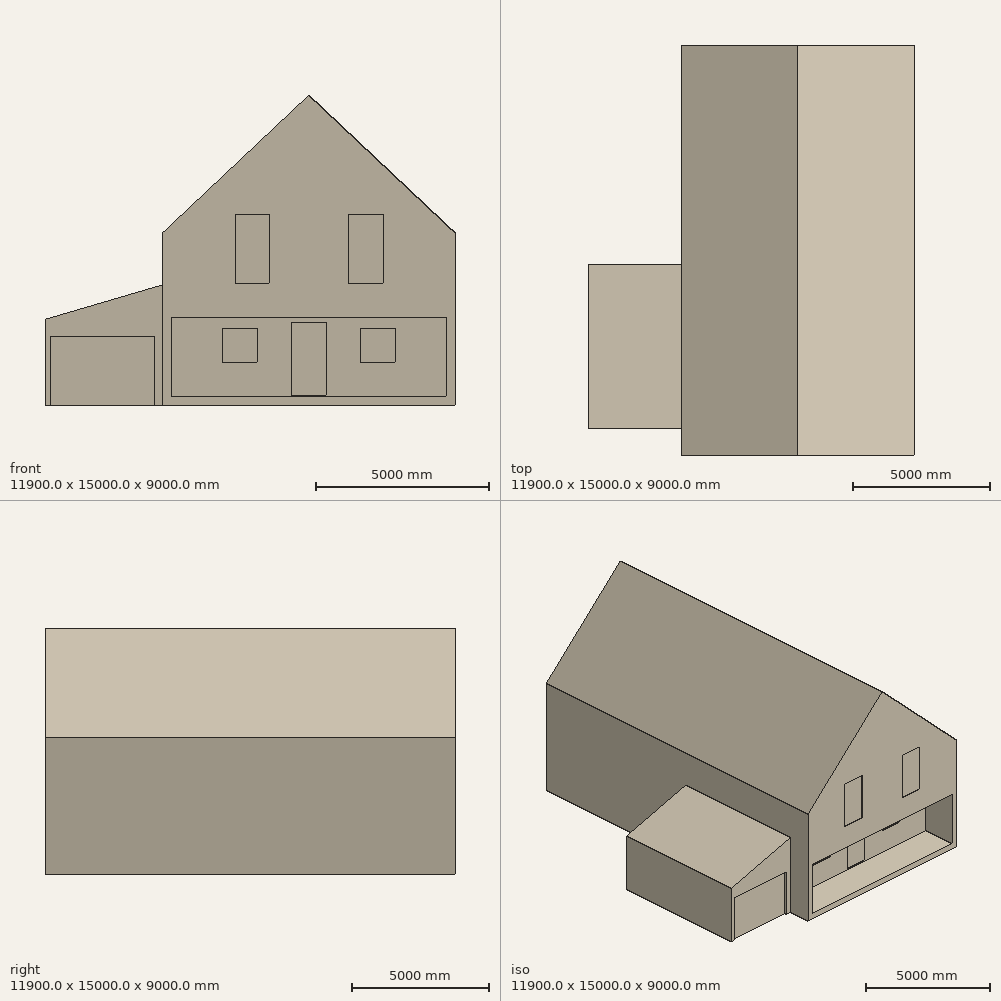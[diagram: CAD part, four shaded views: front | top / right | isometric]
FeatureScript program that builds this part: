
annotation { "Feature Type Name" : "Feature", "Feature Type Description" : "" }
export const myFeature = defineFeature(function(context is Context, id is Id, definition is map)
    precondition{}
    {
        {
            var Q0;
            Q0=qCreatedBy(makeId("Top.planeOp"),FACE);
            var sketch = newSketch(context, id + "F0", { "sketchPlane" : qUnion([Q0])});
            skLineSegment(sketch, "E0.bottom", {"start": v(-7500, 17500) * mm, "end": v(7500, 17500) * mm});
            skLineSegment(sketch, "E0.top", {"start": v(-7500, -17500) * mm, "end": v(7500, -17500) * mm});
            skLineSegment(sketch, "E0.left", {"start": v(-7500, 17500) * mm, "end": v(-7500, -17500) * mm});
            skLineSegment(sketch, "E0.right", {"start": v(7500, 17500) * mm, "end": v(7500, -17500) * mm});
            skPoint(sketch, "E0.middle", {"position": v(0, 0) * mm});
            skLineSegment(sketch, "E1.bottom", {"start": v(-3400, 2500) * mm, "end": v(5100, 2500) * mm});
            skLineSegment(sketch, "E1.top", {"start": v(-3400, -12500) * mm, "end": v(5100, -12500) * mm});
            skLineSegment(sketch, "E1.left", {"start": v(-3400, 2500) * mm, "end": v(-3400, -12500) * mm});
            skLineSegment(sketch, "E1.right", {"start": v(5100, 2500) * mm, "end": v(5100, -12500) * mm});
            skSolve(sketch);
        }
        {
            var Q0;
            Q0=makeQuery(id+"F0.imprint","IMPRINT",FACE,{"disambiguationData":[TD([[makeQuery(id+"F0.imprint","IMPRINT",EDGE,{"derivedFrom":sQuery(id+"F0.wireOp",EDGE,"E1.bottom")}),-1.0]])]});
            extrude(context, id + "F1", {"entities" : qUnion([Q0]), "depth" : 5000 * mm, "offsetDistance" : 25 * mm});
        }
        {
            var Q0;
            Q0=makeQuery(id+"F1.opExtrude","SWEPT_FACE",FACE,{"disambiguationData":[OSD([sQuery(id+"F0.wireOp",EDGE,"E1.top")])]});
            var sketch = newSketch(context, id + "F2", { "sketchPlane" : qUnion([Q0])});
            skLineSegment(sketch, "E2", {"start": v(-3400, 5000) * mm, "end": v(850, 9000) * mm});
            skLineSegment(sketch, "E3", {"start": v(850, 9000) * mm, "end": v(5100, 5000) * mm});
            skLineSegment(sketch, "E4", {"start": v(5100, 5000) * mm, "end": v(-3400, 5000) * mm});
            skSolve(sketch);
        }
        {
            var Q0;
            Q0=makeQuery(id+"F2.imprint","IMPRINT",FACE,{"disambiguationData":[TD([[makeQuery(id+"F2.imprint","IMPRINT",EDGE,{"derivedFrom":sQuery(id+"F2.wireOp",EDGE,"E2")}),-1.0]])]});
            extrude(context, id + "F3", {"entities" : qUnion([Q0]), "operationType" : NewBodyOperationType.ADD, "oppositeDirection" : true, "depth" : 15000 * mm, "offsetDistance" : 25 * mm});
        }
        {
            var Q0;
            Q0=makeQuery(id+"F3.boolean.opBoolean","MERGE",FACE,{"derivedFrom":[makeQuery(id+"F1.opExtrude","SWEPT_FACE",FACE,{"disambiguationData":[OSD([sQuery(id+"F0.wireOp",EDGE,"E1.top")])]}),makeQuery(id+"F3.opExtrude","CAP_FACE",FACE,{"disambiguationData":[OSD([sQuery(id+"F2.wireOp",EDGE,"E2"),sQuery(id+"F2.wireOp",EDGE,"E3"),sQuery(id+"F2.wireOp",EDGE,"E4")])],"isStart":true})]});
            var sketch = newSketch(context, id + "F4", { "sketchPlane" : qUnion([Q0])});
            skLineSegment(sketch, "E5", {"start": v(-6800, 2500) * mm, "end": v(-3400, 3500) * mm});
            skLineSegment(sketch, "E6", {"start": v(-3400, 3500) * mm, "end": v(-3400, 0) * mm});
            skLineSegment(sketch, "E7", {"start": v(-3400, 0) * mm, "end": v(-6800, 0) * mm});
            skLineSegment(sketch, "E8", {"start": v(-6800, 0) * mm, "end": v(-6800, 2500) * mm});
            skSolve(sketch);
        }
        {
            var Q0;
            Q0 = qSketchRegion(id + "F4", true);
            var Q1;
            {var subQ0=sQuery(id+"F4.wireOp",EDGE,"E5");Q1=makeQuery(id+"F4.imprint","IMPRINT",FACE,{"disambiguationData":[TD([[makeQuery(id+"F4.imprint","IMPRINT",EDGE,{"derivedFrom":subQ0}),-1.0]])]});}
            extrude(context, id + "F5", {"entities" : qUnion([Q0, Q1]), "operationType" : NewBodyOperationType.ADD, "oppositeDirection" : true, "depth" : 7000 * mm, "offsetDistance" : 25 * mm, "hasSecondDirection" : true, "secondDirectionOppositeDirection" : true, "secondDirectionDepth" : 1000 * mm});
        }
        {
            var Q0;
            Q0=makeQuery(id+"F5.opExtrude","CAP_FACE",FACE,{"disambiguationData":[OSD([sQuery(id+"F4.wireOp",EDGE,"E5"),sQuery(id+"F4.wireOp",EDGE,"E6"),sQuery(id+"F4.wireOp",EDGE,"E7"),sQuery(id+"F4.wireOp",EDGE,"E8")])],"isStart":true});
            var sketch = newSketch(context, id + "F6", { "sketchPlane" : qUnion([Q0])});
            skLineSegment(sketch, "E9", {"start": v(-6650, 0) * mm, "end": v(-6650, 2000) * mm});
            skLineSegment(sketch, "E10", {"start": v(-6650, 2000) * mm, "end": v(-3650, 2000) * mm});
            skLineSegment(sketch, "E11", {"start": v(-3650, 2000) * mm, "end": v(-3650, 0) * mm});
            skSolve(sketch);
        }
        {
            var Q0;
            {var subQ0=sQuery(id+"F6.wireOp",EDGE,"E9");Q0=makeQuery(id+"F6.imprint","IMPRINT",FACE,{"disambiguationData":[TD([[makeQuery(id+"F6.imprint","IMPRINT",EDGE,{"derivedFrom":subQ0}),-1.0]])]});}
            extrude(context, id + "F7", {"entities" : qUnion([Q0]), "operationType" : NewBodyOperationType.REMOVE, "oppositeDirection" : true, "depth" : 100 * mm, "offsetDistance" : 25 * mm});
        }
        {
            var Q0;
            Q0=makeQuery(id+"F3.boolean.opBoolean","MERGE",FACE,{"derivedFrom":[makeQuery(id+"F1.opExtrude","SWEPT_FACE",FACE,{"disambiguationData":[OSD([sQuery(id+"F0.wireOp",EDGE,"E1.top")])]}),makeQuery(id+"F3.opExtrude","CAP_FACE",FACE,{"disambiguationData":[OSD([sQuery(id+"F2.wireOp",EDGE,"E2"),sQuery(id+"F2.wireOp",EDGE,"E3"),sQuery(id+"F2.wireOp",EDGE,"E4")])],"isStart":true})]});
            var sketch = newSketch(context, id + "F8", { "sketchPlane" : qUnion([Q0])});
            skSolve(sketch);
        }
        {
            var Q0;
            {var subQ0=sQuery(id+"F0.wireOp",EDGE,"E1.top");Q0=makeQuery(id+"F8.imprint","IMPRINT",FACE,{"disambiguationData":[TD([[makeQuery(id+"F8.imprint","IMPRINT",EDGE,{"derivedFrom":makeQuery(id+"F1.opExtrude","CAP_EDGE",EDGE,{"disambiguationData":[OSD([subQ0])],"isStart":true})}),1.0]])]});}
            var sketch = newSketch(context, id + "F9", { "sketchPlane" : qUnion([Q0])});
            skLineSegment(sketch, "E12.bottom", {"start": v(4850, 250) * mm, "end": v(-3150, 250) * mm});
            skLineSegment(sketch, "E12.top", {"start": v(4850, 2550) * mm, "end": v(-3150, 2550) * mm});
            skLineSegment(sketch, "E12.left", {"start": v(4850, 250) * mm, "end": v(4850, 2550) * mm});
            skLineSegment(sketch, "E12.right", {"start": v(-3150, 250) * mm, "end": v(-3150, 2550) * mm});
            skSolve(sketch);
        }
        {
            var Q0;
            Q0=makeQuery(id+"F9.imprint","IMPRINT",FACE,{"disambiguationData":[TD([[makeQuery(id+"F9.imprint","IMPRINT",EDGE,{"derivedFrom":sQuery(id+"F9.wireOp",EDGE,"E12.bottom")}),-1.0]])]});
            extrude(context, id + "F10", {"entities" : qUnion([Q0]), "operationType" : NewBodyOperationType.REMOVE, "oppositeDirection" : true, "depth" : 1500 * mm, "offsetDistance" : 25 * mm});
        }
        {
            var Q0;
            Q0=makeQuery(id+"F10.boolean.opBoolean","COPY",FACE,{"derivedFrom":makeQuery(id+"F10.opExtrude","CAP_FACE",FACE,{"disambiguationData":[OSD([sQuery(id+"F9.wireOp",EDGE,"E12.bottom"),sQuery(id+"F9.wireOp",EDGE,"E12.top"),sQuery(id+"F9.wireOp",EDGE,"E12.left"),sQuery(id+"F9.wireOp",EDGE,"E12.right")])],"isStart":false})});
            var sketch = newSketch(context, id + "F11", { "sketchPlane" : qUnion([Q0])});
            skLineSegment(sketch, "E13.bottom", {"start": v(350, 2400) * mm, "end": v(1350, 2400) * mm});
            skLineSegment(sketch, "E13.top", {"start": v(350, 300) * mm, "end": v(1350, 300) * mm});
            skLineSegment(sketch, "E13.left", {"start": v(350, 2400) * mm, "end": v(350, 300) * mm});
            skLineSegment(sketch, "E13.right", {"start": v(1350, 2400) * mm, "end": v(1350, 300) * mm});
            skLineSegment(sketch, "E14.bottom", {"start": v(-1650, 2250) * mm, "end": v(-650, 2250) * mm});
            skLineSegment(sketch, "E14.top", {"start": v(-1650, 1250) * mm, "end": v(-650, 1250) * mm});
            skLineSegment(sketch, "E14.left", {"start": v(-1650, 2250) * mm, "end": v(-1650, 1250) * mm});
            skLineSegment(sketch, "E14.right", {"start": v(-650, 2250) * mm, "end": v(-650, 1250) * mm});
            skLineSegment(sketch, "E15.bottom", {"start": v(2350, 2250) * mm, "end": v(3350, 2250) * mm});
            skLineSegment(sketch, "E15.top", {"start": v(2350, 1250) * mm, "end": v(3350, 1250) * mm});
            skLineSegment(sketch, "E15.left", {"start": v(2350, 2250) * mm, "end": v(2350, 1250) * mm});
            skLineSegment(sketch, "E15.right", {"start": v(3350, 2250) * mm, "end": v(3350, 1250) * mm});
            skSolve(sketch);
        }
        {
            var Q0;
            Q0=makeQuery(id+"F11.imprint","IMPRINT",FACE,{"disambiguationData":[TD([[makeQuery(id+"F11.imprint","IMPRINT",EDGE,{"derivedFrom":sQuery(id+"F11.wireOp",EDGE,"E13.bottom")}),-1.0]])]});
            var Q1;
            Q1=makeQuery(id+"F11.imprint","IMPRINT",FACE,{"disambiguationData":[TD([[makeQuery(id+"F11.imprint","IMPRINT",EDGE,{"derivedFrom":sQuery(id+"F11.wireOp",EDGE,"E14.bottom")}),-1.0]])]});
            var Q2;
            Q2=makeQuery(id+"F11.imprint","IMPRINT",FACE,{"disambiguationData":[TD([[makeQuery(id+"F11.imprint","IMPRINT",EDGE,{"derivedFrom":sQuery(id+"F11.wireOp",EDGE,"E15.bottom")}),-1.0]])]});
            extrude(context, id + "F12", {"entities" : qUnion([Q0, Q1, Q2]), "operationType" : NewBodyOperationType.REMOVE, "oppositeDirection" : true, "depth" : 25 * mm, "offsetDistance" : 25 * mm});
        }
        {
            var Q0;
            Q0=makeQuery(id+"F3.boolean.opBoolean","MERGE",FACE,{"derivedFrom":[makeQuery(id+"F1.opExtrude","SWEPT_FACE",FACE,{"disambiguationData":[OSD([sQuery(id+"F0.wireOp",EDGE,"E1.top")])]}),makeQuery(id+"F3.opExtrude","CAP_FACE",FACE,{"disambiguationData":[OSD([sQuery(id+"F2.wireOp",EDGE,"E2"),sQuery(id+"F2.wireOp",EDGE,"E3"),sQuery(id+"F2.wireOp",EDGE,"E4")])],"isStart":true})]});
            var sketch = newSketch(context, id + "F13", { "sketchPlane" : qUnion([Q0])});
            skLineSegment(sketch, "E16.bottom", {"start": v(-1300, 5550) * mm, "end": v(-300, 5550) * mm});
            skLineSegment(sketch, "E16.top", {"start": v(-1300, 3550) * mm, "end": v(-300, 3550) * mm});
            skLineSegment(sketch, "E16.left", {"start": v(-1300, 5550) * mm, "end": v(-1300, 3550) * mm});
            skLineSegment(sketch, "E16.right", {"start": v(-300, 5550) * mm, "end": v(-300, 3550) * mm});
            skLineSegment(sketch, "E17.bottom", {"start": v(2000, 5550) * mm, "end": v(3000, 5550) * mm});
            skLineSegment(sketch, "E17.top", {"start": v(2000, 3550) * mm, "end": v(3000, 3550) * mm});
            skLineSegment(sketch, "E17.left", {"start": v(2000, 5550) * mm, "end": v(2000, 3550) * mm});
            skLineSegment(sketch, "E17.right", {"start": v(3000, 5550) * mm, "end": v(3000, 3550) * mm});
            skSolve(sketch);
        }
        {
            var Q0;
            Q0=makeQuery(id+"F13.imprint","IMPRINT",FACE,{"disambiguationData":[TD([[makeQuery(id+"F13.imprint","IMPRINT",EDGE,{"derivedFrom":sQuery(id+"F13.wireOp",EDGE,"E16.bottom")}),-1.0]])]});
            var Q1;
            Q1=makeQuery(id+"F13.imprint","IMPRINT",FACE,{"disambiguationData":[TD([[makeQuery(id+"F13.imprint","IMPRINT",EDGE,{"derivedFrom":sQuery(id+"F13.wireOp",EDGE,"E17.bottom")}),-1.0]])]});
            extrude(context, id + "F14", {"entities" : qUnion([Q0, Q1]), "operationType" : NewBodyOperationType.REMOVE, "oppositeDirection" : true, "depth" : 25 * mm, "offsetDistance" : 25 * mm});
        }
        {
            var Q0;
            Q0=makeQuery(id+"F3.boolean.opBoolean","MERGE",FACE,{"derivedFrom":[makeQuery(id+"F1.opExtrude","SWEPT_FACE",FACE,{"disambiguationData":[OSD([sQuery(id+"F0.wireOp",EDGE,"E1.bottom")])]}),makeQuery(id+"F3.opExtrude","CAP_FACE",FACE,{"disambiguationData":[OSD([sQuery(id+"F2.wireOp",EDGE,"E2"),sQuery(id+"F2.wireOp",EDGE,"E3"),sQuery(id+"F2.wireOp",EDGE,"E4")])],"isStart":false})]});
            var sketch = newSketch(context, id + "F15", { "sketchPlane" : qUnion([Q0])});
            skLineSegment(sketch, "E18", {"start": v(-5100, 0) * mm, "end": v(-5100, 5000) * mm});
            skLineSegment(sketch, "E19", {"start": v(-5100, 5000) * mm, "end": v(-850, 9000) * mm});
            skLineSegment(sketch, "E20", {"start": v(-850, 9000) * mm, "end": v(3400, 5000) * mm});
            skLineSegment(sketch, "E21", {"start": v(3400, 5000) * mm, "end": v(3400, 0) * mm});
            skLineSegment(sketch, "E22", {"start": v(3400, 0) * mm, "end": v(-5100, 0) * mm});
            skLineSegment(sketch, "E23.0", {"start": v(-850, 8588.03) * mm, "end": v(3100, 4870.38) * mm});
            skLineSegment(sketch, "E23.1", {"start": v(-4800, 4870.38) * mm, "end": v(-850, 8588.03) * mm});
            skLineSegment(sketch, "E23.2", {"start": v(3100, 4870.38) * mm, "end": v(3100, 300) * mm});
            skLineSegment(sketch, "E23.3", {"start": v(3100, 300) * mm, "end": v(-4800, 300) * mm});
            skLineSegment(sketch, "E23.4", {"start": v(-4800, 300) * mm, "end": v(-4800, 4870.38) * mm});
            skSolve(sketch);
        }
        {
            var Q0;
            Q0=makeQuery(id+"F15.imprint","IMPRINT",FACE,{"disambiguationData":[TD([[makeQuery(id+"F15.imprint","IMPRINT",EDGE,{"derivedFrom":sQuery(id+"F15.wireOp",EDGE,"E23.0")}),-1.0]])]});
            extrude(context, id + "F16", {"entities" : qUnion([Q0]), "operationType" : NewBodyOperationType.REMOVE, "oppositeDirection" : true, "depth" : 1000 * mm, "offsetDistance" : 25 * mm});
        }
    });
